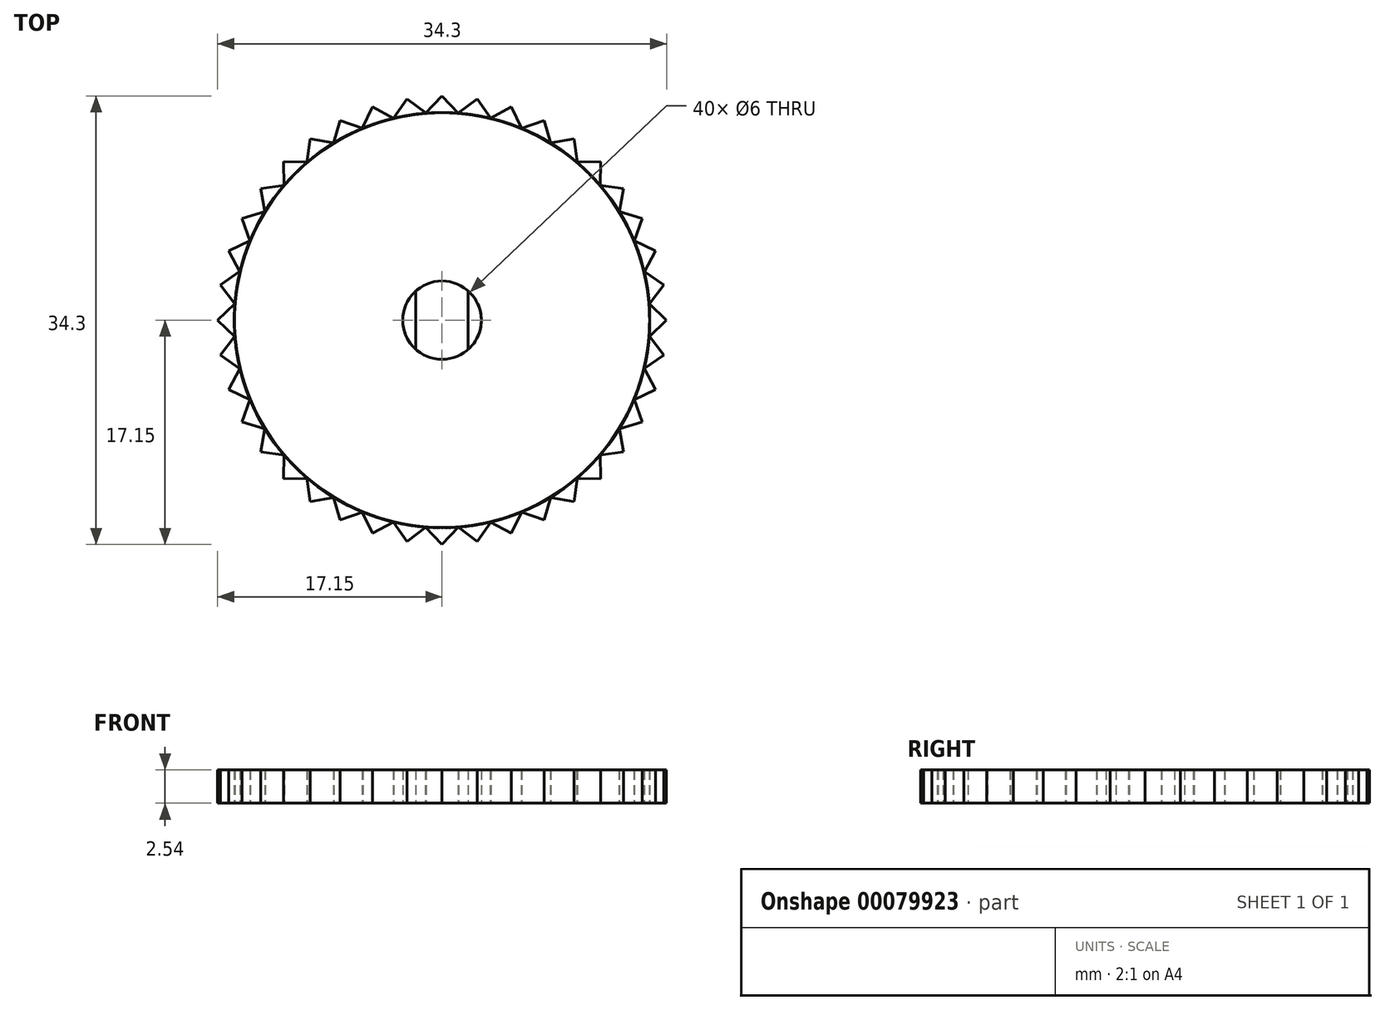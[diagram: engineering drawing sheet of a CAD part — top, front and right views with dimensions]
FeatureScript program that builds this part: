
annotation { "Feature Type Name" : "Feature", "Feature Type Description" : "" }
export const myFeature = defineFeature(function(context is Context, id is Id, definition is map)
    precondition{}
    {
        {
            var Q0;
            Q0=qCreatedBy(makeId("Top.planeOp"),FACE);
            var sketch = newSketch(context, id + "F0", { "sketchPlane" : qUnion([Q0])});
            skCircle(sketch, "E0", {"center": v(0, 0) * mm, "radius": 15.88 * mm});
            skLineSegment(sketch, "E1", {"start": v(-15.82, -1.27) * mm, "end": v(-17.14, 0) * mm});
            skLineSegment(sketch, "E2", {"start": v(-17.14, 0) * mm, "end": v(-15.82, 1.27) * mm});
            skCircle(sketch, "E3", {"center": v(0, 0) * mm, "radius": 3 * mm});
            skLineSegment(sketch, "E4", {"start": v(2, -2.24) * mm, "end": v(2, 2.24) * mm});
            skLineSegment(sketch, "E5", {"start": v(-2, -2.24) * mm, "end": v(-2, 2.24) * mm});
            skSolve(sketch);
        }
        {
            var Q0;
            Q0=makeQuery(id+"F0.imprint","IMPRINT",FACE,{"disambiguationData":[TD([[makeQuery(id+"F0.imprint","IMPRINT",EDGE,{"derivedFrom":sQuery(id+"F0.wireOp",EDGE,"E0")}),1.0]])]});
            var Q1;
            {var subQ0=sQuery(id+"F0.wireOp",EDGE,"1KidRQuU-K3oB-VxLJ-RmBU-VO4mWQVhBok9");Q1=makeQuery(id+"F0.imprint","IMPRINT",FACE,{"disambiguationData":[TD([[makeQuery(id+"F0.imprint","IMPRINT",EDGE,{"derivedFrom":subQ0}),1.0]])]});}
            var Q2;
            {var subQ0=sQuery(id+"F0.wireOp",EDGE,"UtIkhQJM-1GxF-WafV-xQUZ-pODcofbWjBiq");Q2=makeQuery(id+"F0.imprint","IMPRINT",FACE,{"disambiguationData":[TD([[makeQuery(id+"F0.imprint","IMPRINT",EDGE,{"derivedFrom":subQ0}),-1.0]])]});}
            extrude(context, id + "F1", {"entities" : qUnion([Q0, Q1, Q2]), "depth" : 2.54 * mm});
        }
        {
            var Q0;
            {var subQ0=sQuery(id+"F0.wireOp",EDGE,"E1");Q0=makeQuery(id+"F0.imprint","IMPRINT",FACE,{"disambiguationData":[TD([[makeQuery(id+"F0.imprint","IMPRINT",EDGE,{"derivedFrom":subQ0}),-1.0]])]});}
            extrude(context, id + "F2", {"entities" : qUnion([Q0]), "operationType" : NewBodyOperationType.ADD, "depth" : 2.54 * mm});
        }
        {
            var Q0;
            Q0=makeQuery(id+"F1.opExtrude","SWEPT_BODY",BODY,{"disambiguationData":[OSD([sQuery(id+"F0.wireOp",EDGE,"E0")])]});
            var Q1;
            Q1=makeQuery(id+"F1.opExtrude","SWEPT_FACE",FACE,{"disambiguationData":[OSD([sQuery(id+"F0.wireOp",EDGE,"E0")])]});
            circularPattern(context, id + "F3", {"entities" : qUnion([Q0]), "axis" : qUnion([Q1]), "angle" : 9 * degree, "instanceCount" : 40});
        }
        {
            var Q0;
            {var subQ0=sQuery(id+"F0.wireOp",EDGE,"E5");Q0=makeQuery(id+"F0.imprint","IMPRINT",FACE,{"disambiguationData":[TD([[makeQuery(id+"F0.imprint","IMPRINT",EDGE,{"derivedFrom":subQ0}),1.0]])]});}
            var Q1;
            {var subQ0=sQuery(id+"F0.wireOp",EDGE,"E4");Q1=makeQuery(id+"F0.imprint","IMPRINT",FACE,{"disambiguationData":[TD([[makeQuery(id+"F0.imprint","IMPRINT",EDGE,{"derivedFrom":subQ0}),-1.0]])]});}
            extrude(context, id + "F4", {"entities" : qUnion([Q0, Q1]), "depth" : 2.54 * mm});
        }
    });
